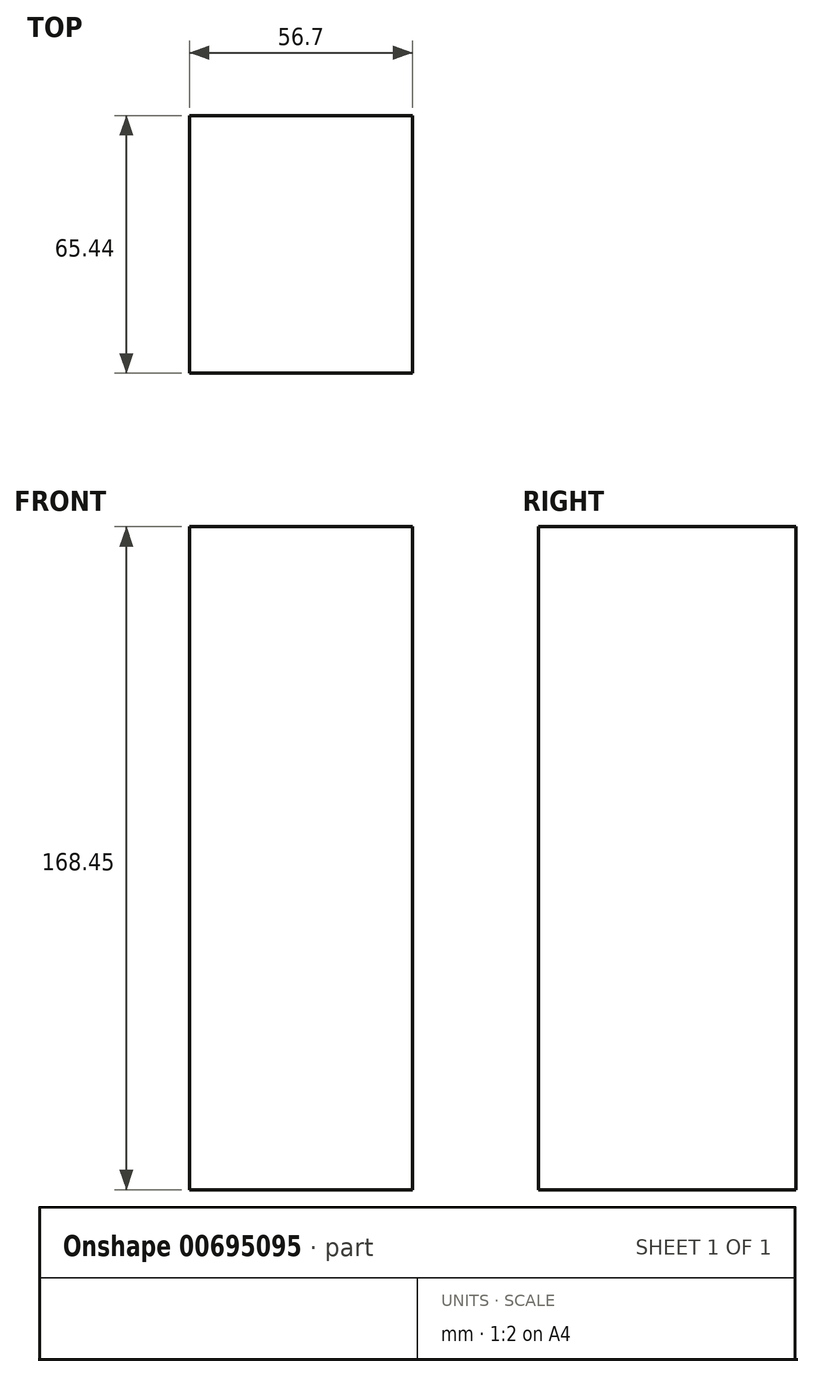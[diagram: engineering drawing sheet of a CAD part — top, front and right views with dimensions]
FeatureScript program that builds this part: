
annotation { "Feature Type Name" : "Feature", "Feature Type Description" : "" }
export const myFeature = defineFeature(function(context is Context, id is Id, definition is map)
    precondition{}
    {
        {
            var Q0;
            Q0=qCreatedBy(makeId("Top.planeOp"),FACE);
            var sketch = newSketch(context, id + "F0", { "sketchPlane" : qUnion([Q0])});
            skLineSegment(sketch, "E0.bottom", {"start": v(0, 0) * mm, "end": v(56.7, 0) * mm});
            skLineSegment(sketch, "E0.top", {"start": v(0, -65.44) * mm, "end": v(56.7, -65.44) * mm});
            skLineSegment(sketch, "E0.left", {"start": v(0, 0) * mm, "end": v(0, -65.44) * mm});
            skLineSegment(sketch, "E0.right", {"start": v(56.7, 0) * mm, "end": v(56.7, -65.44) * mm});
            skSolve(sketch);
        }
        {
            var Q0;
            Q0=makeQuery(id+"F0.imprint","IMPRINT",FACE,{"disambiguationData":[TD([[makeQuery(id+"F0.imprint","IMPRINT",EDGE,{"derivedFrom":sQuery(id+"F0.wireOp",EDGE,"E0.bottom")}),-1.0]])]});
            extrude(context, id + "F1", {"entities" : qUnion([Q0]), "depth" : 168.45 * mm, "offsetDistance" : 25 * mm});
        }
    });
